# Revit family: 048530
name_source: partatom
category: Electrical Fixtures
revit_build: Autodesk Revit 2017 (Build: 20160225_1515(x64)
units: mm (PartAtom-declared; Revit-internal decimal feet)

## family parameters
Cut with Voids When Loaded = No
Host = Face
Maintain Annotation Orientation = Yes
Part Type = Normal
Room Calculation Point = No
Round Connector Dimension = Use Diameter
Shared = No

## types (1)
- Sock. earth pin HC + SH WP surface-mounted grey
    Available = No
    BIM (1) = https://media.stage.bim.site
    Category = Socket outlet
    Data sheet (1) = https://katalog.gira.de
    Default Elevation = 1219 mm
    Description = Sock.pin HC SH WP SM GY,Socket outlet with earth pin 16 A 250 V~ with hinged cover, integrated increased contact protection (shutter) and symbol ,,grey,Features:,- With screw terminals.,,Notes :,- Approved in compliance with NF C 61-314 (2003).,- Increased contact protection pursuant to DIN-VDE 0620-1.
    GTIN = 4010337485308
    HAN = 048530
    HeinzeBIM = https://bimportal.heinze.de
    Manufacturer = Gira
    Manufacturer URL = https://www.gira.de
    Model = Other
    Name = Sock. earth pin HC + SH WP surface-mounted grey
    Number of active Pins (round) = 1
    Transparent = No
    URL = http://katalog.gira.de

## geometry (parser evidence)
native form markers: Blend x2, Sweep x3
no freeform markers — native parametric forms only
